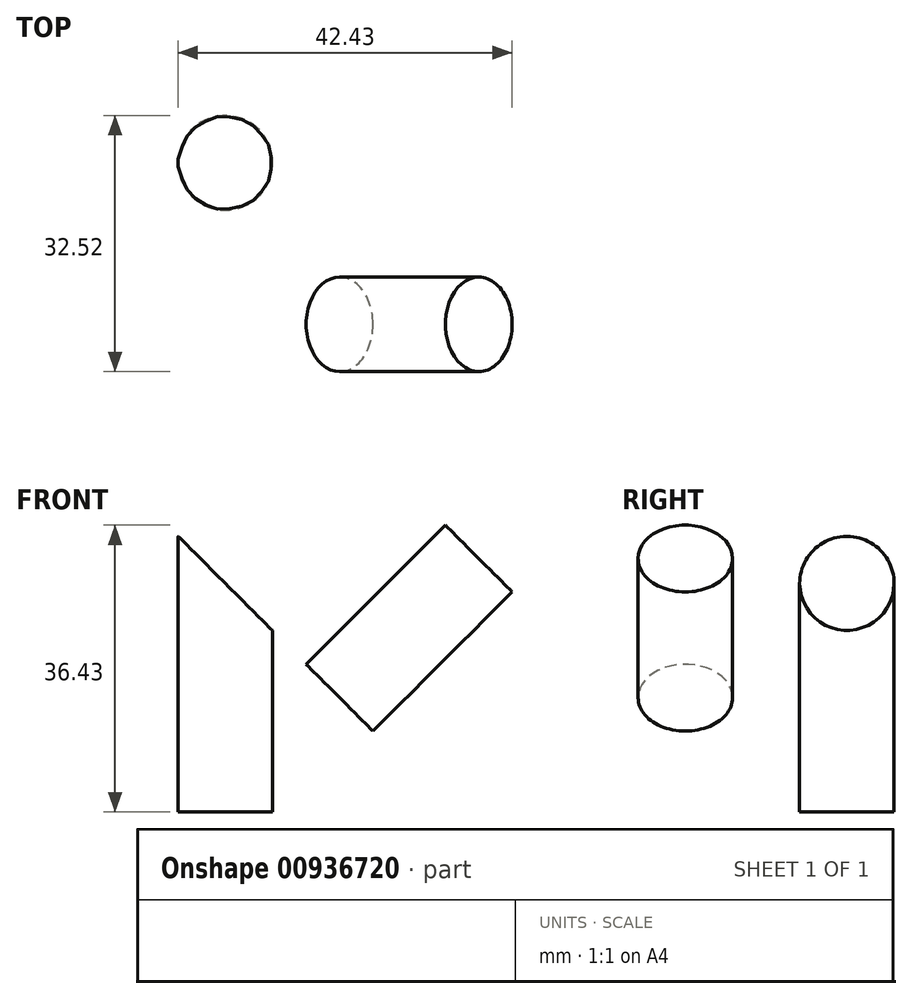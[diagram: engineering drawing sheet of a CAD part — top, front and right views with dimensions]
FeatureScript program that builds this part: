
annotation { "Feature Type Name" : "Feature", "Feature Type Description" : "" }
export const myFeature = defineFeature(function(context is Context, id is Id, definition is map)
    precondition{}
    {
        {
            var Q0;
            Q0=qCreatedBy(makeId("Top.planeOp"),FACE);
            var sketch = newSketch(context, id + "F0", { "sketchPlane" : qUnion([Q0])});
            skCircle(sketch, "E0", {"center": v(0, 0) * mm, "radius": 6 * mm});
            skSolve(sketch);
        }
        {
            var Q0;
            Q0=makeQuery(id+"F0.imprint","IMPRINT",FACE,{"disambiguationData":[TD([[makeQuery(id+"F0.imprint","IMPRINT",EDGE,{"derivedFrom":sQuery(id+"F0.wireOp",EDGE,"E0")}),1.0]])]});
            extrude(context, id + "F1", {"entities" : qUnion([Q0]), "depth" : 35 * mm, "offsetDistance" : 25 * mm});
        }
        {
            var Q0;
            Q0=qCreatedBy(makeId("Front.planeOp"),FACE);
            var sketch = newSketch(context, id + "F2", { "sketchPlane" : qUnion([Q0])});
            skLineSegment(sketch, "E1", {"start": v(-6.05, 35.07) * mm, "end": v(6.12, 35.07) * mm});
            skLineSegment(sketch, "E2", {"start": v(6.12, 35.07) * mm, "end": v(6.12, 22.9) * mm});
            skLineSegment(sketch, "E3", {"start": v(-6.05, 35.07) * mm, "end": v(6.12, 22.9) * mm});
            skSolve(sketch);
        }
        {
            var Q0;
            Q0 = qSketchRegion(id + "F2", true);
            extrude(context, id + "F3", {"entities" : qUnion([Q0]), "operationType" : NewBodyOperationType.REMOVE, "endBound" : BoundingType.SYMMETRIC, "oppositeDirection" : true, "depth" : 25 * mm, "offsetDistance" : 25 * mm});
        }
        {
            var Q0;
            Q0=makeQuery(id+"F3.boolean.opBoolean","COPY",FACE,{"derivedFrom":makeQuery(id+"F3.opExtrude","SWEPT_FACE",FACE,{"disambiguationData":[OSD([sQuery(id+"F2.wireOp",EDGE,"E3")])]})});
            var sketch = newSketch(context, id + "F4", { "sketchPlane" : qUnion([Q0])});
            skCircle(sketch, "E4", {"center": v(-20.52, 0) * mm, "radius": 6 * mm});
            skSolve(sketch);
        }
        {
            var Q0;
            {var subQ0=sQuery(id+"F4.wireOp",EDGE,"E4");var subQ1=makeQuery(id+"F3.boolean.opBoolean","INTERSECT",EDGE,{"derivedFrom":[makeQuery(id+"F1.opExtrude","SWEPT_FACE",FACE,{"disambiguationData":[OSD([sQuery(id+"F0.wireOp",EDGE,"E0")])]}),makeQuery(id+"F3.opExtrude","SWEPT_FACE",FACE,{"disambiguationData":[OSD([sQuery(id+"F2.wireOp",EDGE,"E3")])]})]});var subQ2=makeQuery(id+"F4.imprint","INTERSECT",VERTEX,{"disambiguationData":[OD(0.0)],"derivedFrom":[subQ1,subQ0]});Q0=makeQuery(id+"F4.imprint","IMPRINT",FACE,{"disambiguationData":[TD([[makeQuery(id+"F4.imprint","IMPRINT",EDGE,{"disambiguationData":[TD([[subQ2,1.0]])],"derivedFrom":subQ0}),1.0]])]});}
            extrude(context, id + "F5", {"entities" : qUnion([Q0]), "operationType" : NewBodyOperationType.ADD, "depth" : 25 * mm, "offsetDistance" : 25 * mm});
        }
    });
